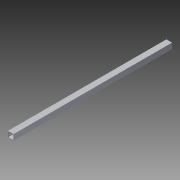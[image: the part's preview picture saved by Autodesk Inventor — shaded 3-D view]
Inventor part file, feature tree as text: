
AUTODESK INVENTOR PART (.ipt)
format: ipt  version: 2013 (Build 170138000, 138)  size: 73,728 bytes
history: native  units: in
note: dims shown in document units (in); Inventor stores cm internally (conversion verified against a paired STEP export)
features: extrude x1, sketch x1
ambient origin geometry x8: Origin, YZ Plane, XZ Plane, XY Plane, X Axis, Y Axis, Z Axis, Center Point
bodies: Solid1 (feature_tree)
feature tree (2):
  extrude  "Extrusion1"  Depth=1.0in
  sketch  "Sketch1"  dims[d0=1.0in d2=1.0in d3=0.0625in d4=28.0in d5=0.0in]
